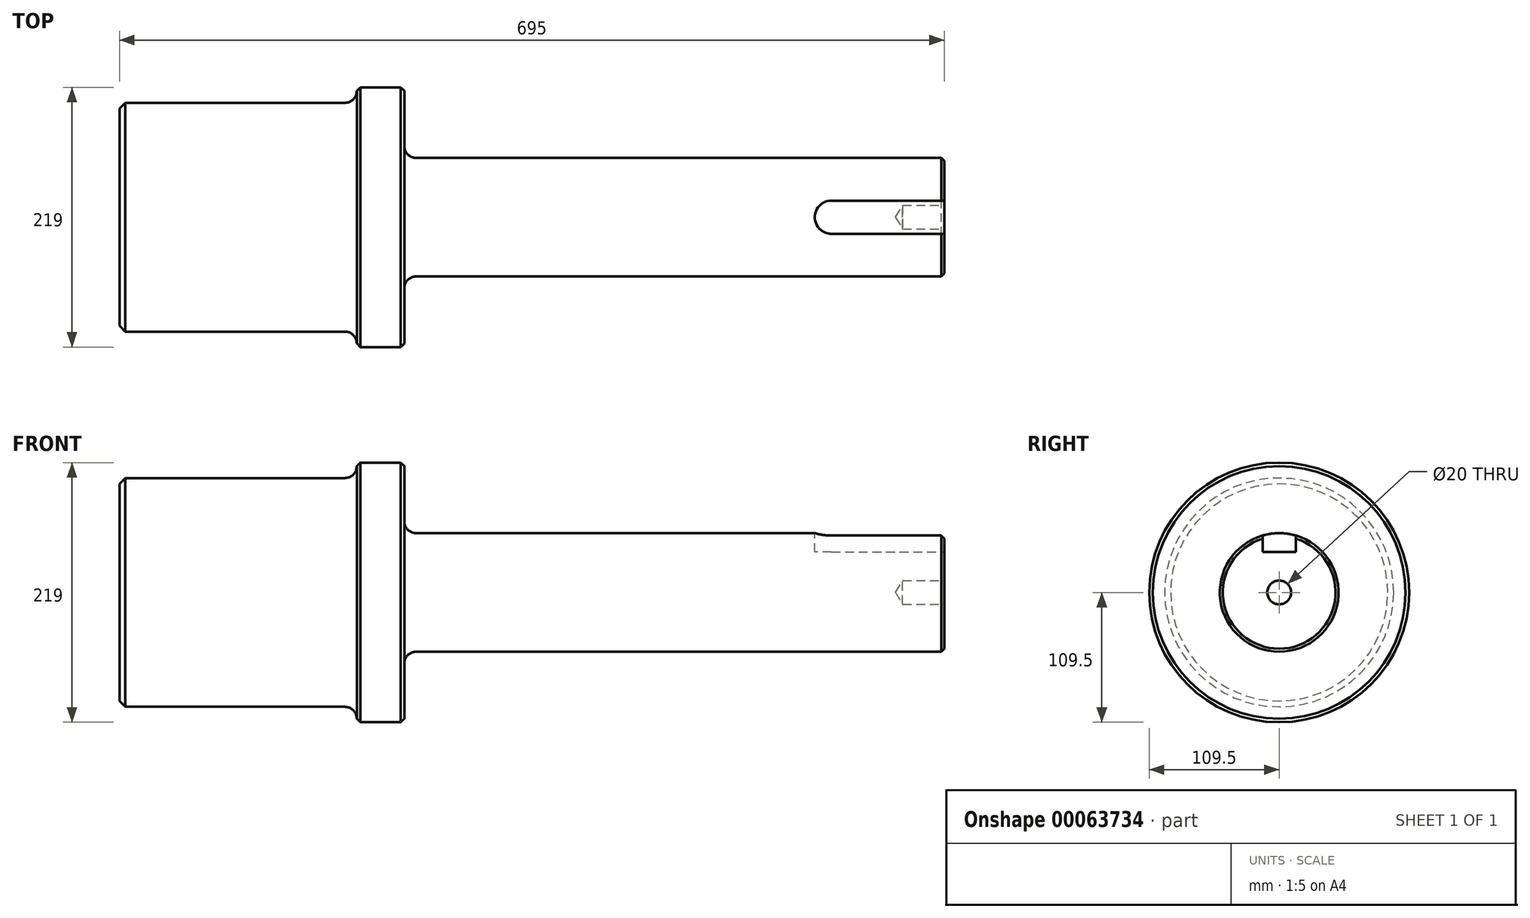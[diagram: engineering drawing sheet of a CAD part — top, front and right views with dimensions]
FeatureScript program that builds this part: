
annotation { "Feature Type Name" : "Feature", "Feature Type Description" : "" }
export const myFeature = defineFeature(function(context is Context, id is Id, definition is map)
    precondition{}
    {
        {
            var Q0;
            Q0=qCreatedBy(makeId("Front.planeOp"),FACE);
            var sketch = newSketch(context, id + "F0", { "sketchPlane" : qUnion([Q0])});
            skLineSegment(sketch, "E0", {"start": v(0, 0) * mm, "end": v(0, 96.5) * mm});
            skLineSegment(sketch, "E1", {"start": v(0, 96.5) * mm, "end": v(200, 96.5) * mm});
            skLineSegment(sketch, "E2", {"start": v(200, 96.5) * mm, "end": v(200, 109.5) * mm});
            skLineSegment(sketch, "E3", {"start": v(200, 109.5) * mm, "end": v(240, 109.5) * mm});
            skLineSegment(sketch, "E4", {"start": v(240, 109.5) * mm, "end": v(240, 50) * mm});
            skLineSegment(sketch, "E5", {"start": v(695, 50) * mm, "end": v(240, 50) * mm});
            skLineSegment(sketch, "E6", {"start": v(695, 50) * mm, "end": v(695, 0) * mm});
            skLineSegment(sketch, "E7", {"start": v(0, 0) * mm, "end": v(695, 0) * mm});
            skSolve(sketch);
        }
        {
            var Q0;
            Q0=makeQuery(id+"F0.imprint","IMPRINT",FACE,{"disambiguationData":[TD([[makeQuery(id+"F0.imprint","IMPRINT",EDGE,{"derivedFrom":sQuery(id+"F0.wireOp",EDGE,"E0")}),-1.0]])]});
            var Q1;
            Q1=sQuery(id+"F0.wireOp",EDGE,"E7");
            revolve(context, id + "F1", {"entities" : qUnion([Q0]), "axis" : qUnion([Q1]), "revolveType" : RevolveType.FULL});
        }
        {
            var Q0;
            Q0=makeQuery(id+"F1.opRevolve","SWEPT_EDGE",EDGE,{"disambiguationData":[OSD([sQuery(id+"F0.wireOp",EDGE,"E4"),sQuery(id+"F0.wireOp",EDGE,"E5")])]});
            var Q1;
            Q1=makeQuery(id+"F1.opRevolve","SWEPT_EDGE",EDGE,{"disambiguationData":[OSD([sQuery(id+"F0.wireOp",EDGE,"E1"),sQuery(id+"F0.wireOp",EDGE,"E2")])]});
            fillet(context, id + "F2", {"entities" : qUnion([Q0, Q1]), "radius" : 10 * mm, "tangentPropagation" : true, "allowEdgeOverflow" : false});
        }
        {
            var Q0;
            Q0=makeQuery(id+"F1.opRevolve","SWEPT_EDGE",EDGE,{"disambiguationData":[OSD([sQuery(id+"F0.wireOp",EDGE,"E0"),sQuery(id+"F0.wireOp",EDGE,"E1")])]});
            chamfer(context, id + "F3", {"entities" : qUnion([Q0]), "width" : 5 * mm, "tangentPropagation" : true});
        }
        {
            var Q0;
            Q0=makeQuery(id+"F1.opRevolve","SWEPT_EDGE",EDGE,{"disambiguationData":[OSD([sQuery(id+"F0.wireOp",EDGE,"E2"),sQuery(id+"F0.wireOp",EDGE,"E3")])]});
            var Q1;
            Q1=makeQuery(id+"F1.opRevolve","SWEPT_EDGE",EDGE,{"disambiguationData":[OSD([sQuery(id+"F0.wireOp",EDGE,"E3"),sQuery(id+"F0.wireOp",EDGE,"E4")])]});
            chamfer(context, id + "F4", {"entities" : qUnion([Q0, Q1]), "width" : 3 * mm, "tangentPropagation" : true});
        }
        {
            var Q0;
            Q0=makeQuery(id+"F1.opRevolve","SWEPT_EDGE",EDGE,{"disambiguationData":[OSD([sQuery(id+"F0.wireOp",EDGE,"E5"),sQuery(id+"F0.wireOp",EDGE,"E6")])]});
            chamfer(context, id + "F5", {"entities" : qUnion([Q0]), "width" : 2.5 * mm, "tangentPropagation" : true});
        }
        {
            var Q0;
            Q0=makeQuery(id+"F1.opRevolve","SWEPT_FACE",FACE,{"disambiguationData":[OSD([sQuery(id+"F0.wireOp",EDGE,"E6")])]});
            var sketch = newSketch(context, id + "F6", { "sketchPlane" : qUnion([Q0])});
            skPoint(sketch, "E8", {"position": v(0, 0) * mm});
            skSolve(sketch);
        }
        {
            var Q0;
            Q0=sQuery(id+"F6.wireOp",VERTEX,"E8");
            var Q1;
            Q1=makeQuery(id+"F1.opRevolve","SWEPT_BODY",BODY,{"disambiguationData":[OSD([sQuery(id+"F0.wireOp",EDGE,"E0"),sQuery(id+"F0.wireOp",EDGE,"E1"),sQuery(id+"F0.wireOp",EDGE,"E2"),sQuery(id+"F0.wireOp",EDGE,"E3"),sQuery(id+"F0.wireOp",EDGE,"E4"),sQuery(id+"F0.wireOp",EDGE,"E5"),sQuery(id+"F0.wireOp",EDGE,"E6"),sQuery(id+"F0.wireOp",EDGE,"E7")])]});
            hole(context, id + "F7", {"style" : HoleStyle.SIMPLE, "holeDiameter" : 20 * mm, "endStyle" : HoleEndStyle.BLIND, "holeDepth" : 35 * mm, "locations" : qUnion([Q0]), "scope" : qUnion([Q1])});
        }
        {
            var Q0;
            Q0=qCreatedBy(makeId("Top.planeOp"),FACE);
            cPlane(context, id + "F8", {"entities" : qUnion([Q0]), "cplaneType" : CPlaneType.OFFSET, "offset" : 50 * mm, "width" : 150 * mm, "height" : 150 * mm});
        }
        {
            var Q0;
            Q0=qCreatedBy(id+"F8.planeOp",FACE);
            var sketch = newSketch(context, id + "F9", { "sketchPlane" : qUnion([Q0])});
            skLineSegment(sketch, "E9.bottom", {"start": v(600, 14) * mm, "end": v(695, 14) * mm});
            skLineSegment(sketch, "E9.top", {"start": v(600, -14) * mm, "end": v(695, -14) * mm});
            skLineSegment(sketch, "E9.right", {"start": v(695, 14) * mm, "end": v(695, -14) * mm});
            skArc(sketch, "E10", {"start": v(600, 14) * mm, "mid": v(586, 0) * mm, "end": v(600, -14) * mm});
            skSolve(sketch);
        }
        {
            var Q0;
            Q0=makeQuery(id+"F9.imprint","IMPRINT",FACE,{"disambiguationData":[TD([[makeQuery(id+"F9.imprint","IMPRINT",EDGE,{"derivedFrom":sQuery(id+"F9.wireOp",EDGE,"E9.bottom")}),-1.0]])]});
            extrude(context, id + "F10", {"entities" : qUnion([Q0]), "operationType" : NewBodyOperationType.REMOVE, "oppositeDirection" : true, "depth" : 16 * mm});
        }
    });
